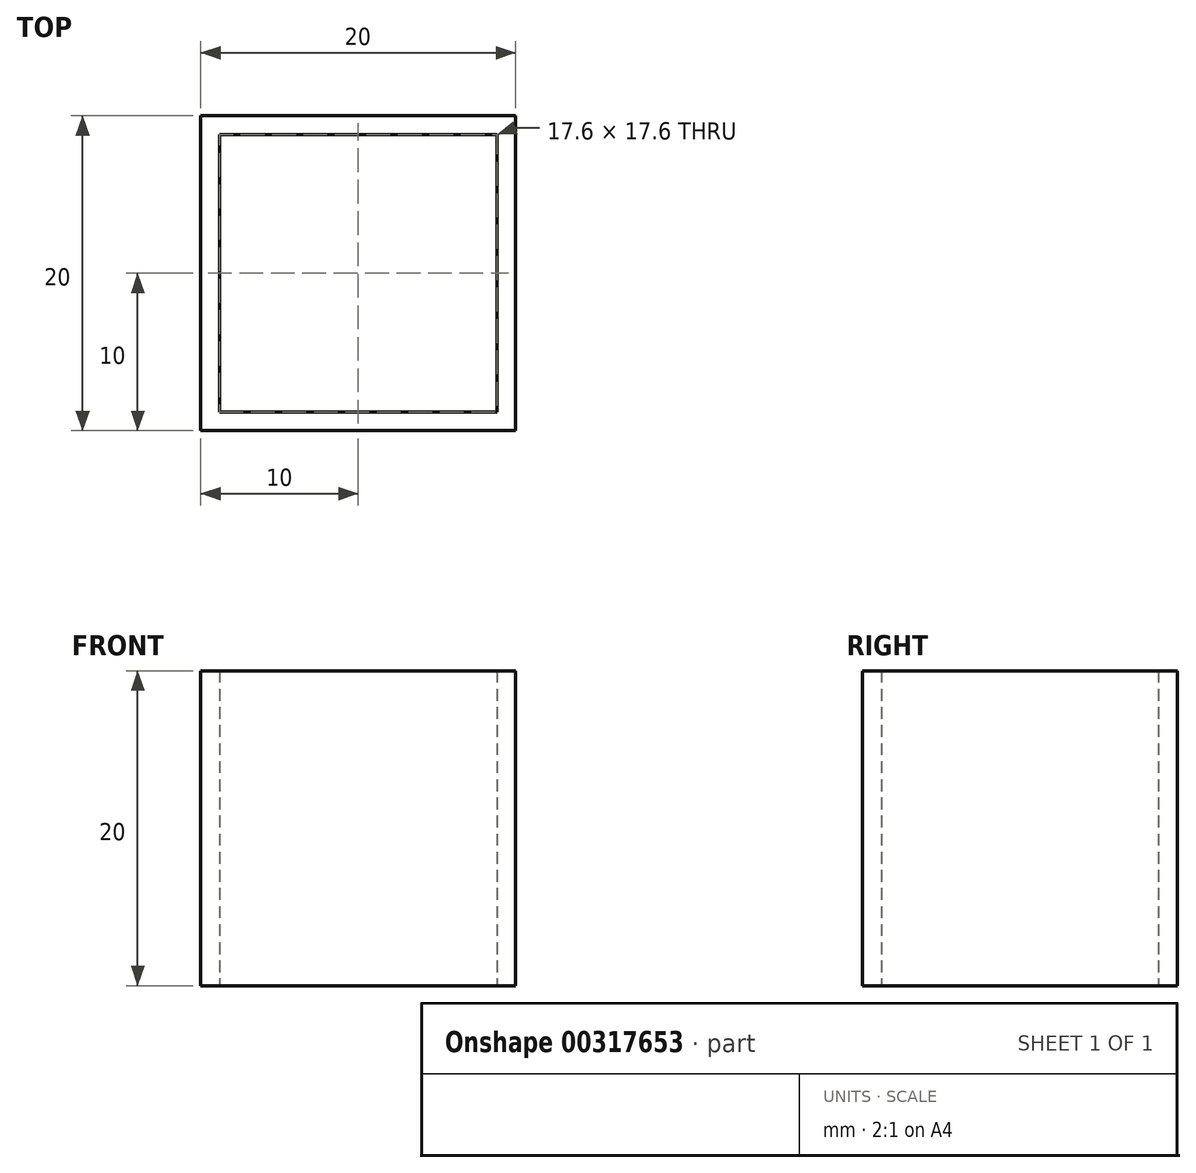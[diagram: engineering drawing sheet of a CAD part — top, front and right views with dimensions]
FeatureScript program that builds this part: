
annotation { "Feature Type Name" : "Feature", "Feature Type Description" : "" }
export const myFeature = defineFeature(function(context is Context, id is Id, definition is map)
    precondition{}
    {
        {
            var Q0;
            Q0=qCreatedBy(makeId("Top.planeOp"),FACE);
            var sketch = newSketch(context, id + "F0", { "sketchPlane" : qUnion([Q0])});
            skLineSegment(sketch, "E0.bottom", {"start": v(-8.8, 8.8) * mm, "end": v(8.8, 8.8) * mm});
            skLineSegment(sketch, "E0.top", {"start": v(-8.8, -8.8) * mm, "end": v(8.8, -8.8) * mm});
            skLineSegment(sketch, "E0.left", {"start": v(-8.8, 8.8) * mm, "end": v(-8.8, -8.8) * mm});
            skLineSegment(sketch, "E0.right", {"start": v(8.8, 8.8) * mm, "end": v(8.8, -8.8) * mm});
            skPoint(sketch, "E0.middle", {"position": v(0, 0) * mm});
            skLineSegment(sketch, "E1.bottom", {"start": v(-10, 10) * mm, "end": v(10, 10) * mm});
            skLineSegment(sketch, "E1.top", {"start": v(-10, -10) * mm, "end": v(10, -10) * mm});
            skLineSegment(sketch, "E1.left", {"start": v(-10, 10) * mm, "end": v(-10, -10) * mm});
            skLineSegment(sketch, "E1.right", {"start": v(10, 10) * mm, "end": v(10, -10) * mm});
            skSolve(sketch);
        }
        {
            var Q0;
            Q0 = qSketchRegion(id + "F0", true);
            extrude(context, id + "F1", {"entities" : qUnion([Q0]), "depth" : 20 * mm, "offsetDistance" : 25 * mm});
        }
    });
